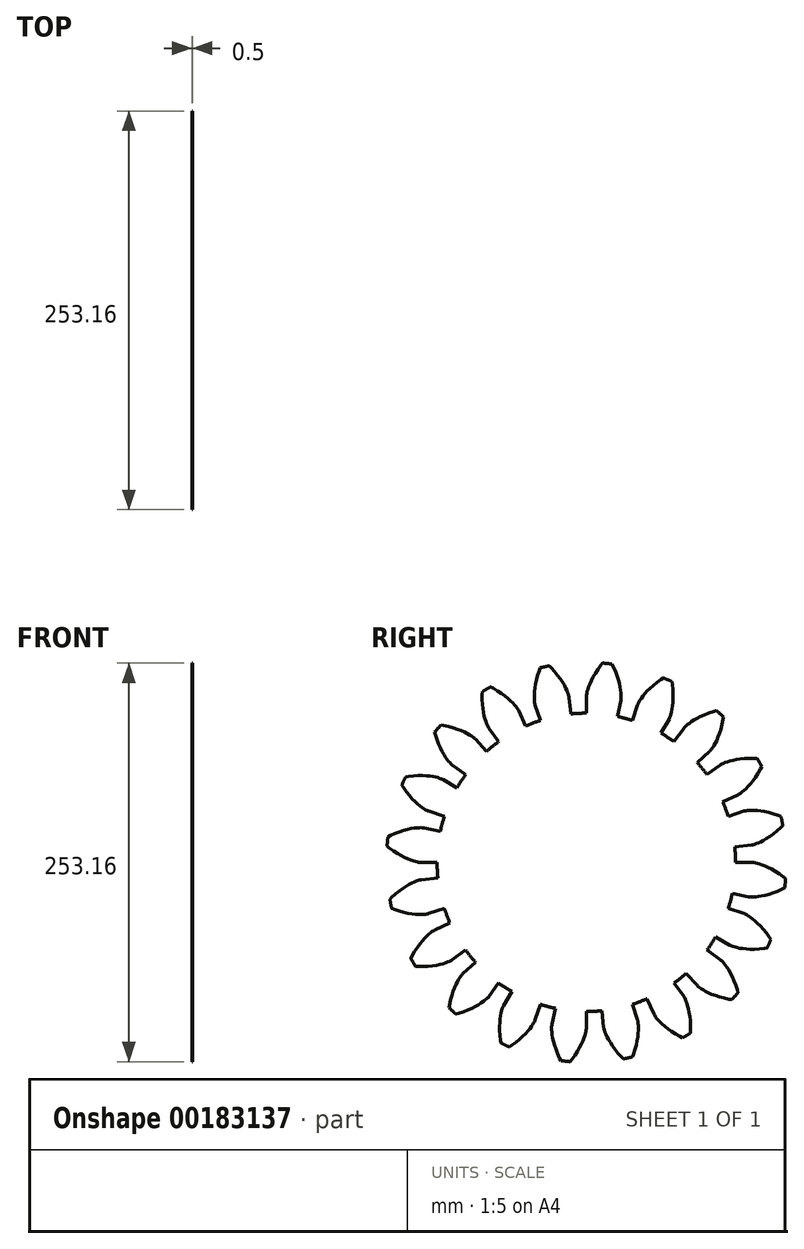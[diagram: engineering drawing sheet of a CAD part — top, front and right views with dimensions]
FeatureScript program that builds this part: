
annotation { "Feature Type Name" : "Feature", "Feature Type Description" : "" }
export const myFeature = defineFeature(function(context is Context, id is Id, definition is map)
    precondition{}
    {
        {
            assignVariable(context, id + "F0", {"name" : "GearThickness", "anyValue" : .5});
        }
        {
            var Q0;
            Q0=qCreatedBy(makeId("Right.planeOp"),FACE);
            var sketch = newSketch(context, id + "F1", { "sketchPlane" : qUnion([Q0])});
            skCircle(sketch, "E0", {"center": v(0, 0) * mm, "radius": 94.77 * mm});
            skCircle(sketch, "E1", {"center": v(0, 0) * mm, "radius": 105.3 * mm, "construction": true});
            skCircle(sketch, "E2", {"center": v(0, 0) * mm, "radius": 112.06 * mm, "construction": true});
            skCircle(sketch, "E3", {"center": v(0, 0) * mm, "radius": 127 * mm});
            skLineSegment(sketch, "E4", {"start": v(0, 0) * mm, "end": v(-105.3, 0) * mm, "construction": true});
            skLineSegment(sketch, "E5.1.0", {"start": v(0, 0) * mm, "end": v(-105.17, 5.26) * mm, "construction": true});
            skLineSegment(sketch, "E5.2.0", {"start": v(0, 0) * mm, "end": v(-104.77, 10.51) * mm, "construction": true});
            skLineSegment(sketch, "E5.3.0", {"start": v(0, 0) * mm, "end": v(-104.12, 15.74) * mm, "construction": true});
            skLineSegment(sketch, "E5.4.0", {"start": v(0, 0) * mm, "end": v(-103.2, 20.92) * mm, "construction": true});
            skLineSegment(sketch, "E5.5.0", {"start": v(0, 0) * mm, "end": v(-102.03, 26.05) * mm, "construction": true});
            skLineSegment(sketch, "E5.6.0", {"start": v(0, 0) * mm, "end": v(-100.6, 31.12) * mm, "construction": true});
            skLineSegment(sketch, "E5.7.0", {"start": v(0, 0) * mm, "end": v(-98.92, 36.1) * mm, "construction": true});
            skLineSegment(sketch, "E5.8.0", {"start": v(0, 0) * mm, "end": v(-96.99, 41) * mm, "construction": true});
            skLineSegment(sketch, "E5.9.0", {"start": v(0, 0) * mm, "end": v(-94.82, 45.8) * mm, "construction": true});
            skLineSegment(sketch, "E5.10.0", {"start": v(0, 0) * mm, "end": v(-92.41, 50.48) * mm, "construction": true});
            skLineSegment(sketch, "E5.11.0", {"start": v(0, 0) * mm, "end": v(-89.77, 55.04) * mm, "construction": true});
            skLineSegment(sketch, "E5.12.0", {"start": v(0, 0) * mm, "end": v(-86.9, 59.46) * mm, "construction": true});
            skLineSegment(sketch, "E5.13.0", {"start": v(0, 0) * mm, "end": v(-83.83, 63.73) * mm, "construction": true});
            skLineSegment(sketch, "E5.14.0", {"start": v(0, 0) * mm, "end": v(-80.54, 67.84) * mm, "construction": true});
            skLineSegment(sketch, "E5.anchor2", {"start": v(0, 0) * mm, "end": v(-80.54, 67.84) * mm, "construction": true});
            skLineSegment(sketch, "E6", {"start": v(-105.17, 5.26) * mm, "end": v(-105.43, 0) * mm, "construction": true});
            skLineSegment(sketch, "E7", {"start": v(-104.77, 10.51) * mm, "end": v(-105.83, 0.04) * mm, "construction": true});
            skLineSegment(sketch, "E8", {"start": v(-104.12, 15.74) * mm, "end": v(-106.48, 0.12) * mm, "construction": true});
            skLineSegment(sketch, "E9", {"start": v(-102.03, 26.05) * mm, "end": v(-108.54, 0.55) * mm, "construction": true});
            skLineSegment(sketch, "E10", {"start": v(-100.6, 31.12) * mm, "end": v(-109.93, 0.94) * mm, "construction": true});
            skLineSegment(sketch, "E11", {"start": v(-98.92, 36.1) * mm, "end": v(-111.55, 1.49) * mm, "construction": true});
            skLineSegment(sketch, "E12", {"start": v(-96.99, 41) * mm, "end": v(-113.4, 2.21) * mm, "construction": true});
            skLineSegment(sketch, "E13", {"start": v(-94.82, 45.8) * mm, "end": v(-115.43, 3.13) * mm, "construction": true});
            skLineSegment(sketch, "E14", {"start": v(-92.41, 50.48) * mm, "end": v(-117.65, 4.28) * mm, "construction": true});
            skLineSegment(sketch, "E15", {"start": v(-89.77, 55.04) * mm, "end": v(-120.04, 5.67) * mm, "construction": true});
            skLineSegment(sketch, "E16", {"start": v(-103.2, 20.92) * mm, "end": v(-107.39, 0.28) * mm, "construction": true});
            skLineSegment(sketch, "E17", {"start": v(-86.9, 59.46) * mm, "end": v(-122.58, 7.31) * mm, "construction": true});
            skLineSegment(sketch, "E18", {"start": v(-83.83, 63.73) * mm, "end": v(-125.25, 9.24) * mm, "construction": true});
            skLineSegment(sketch, "E19", {"start": v(-80.54, 67.84) * mm, "end": v(-128.02, 11.46) * mm, "construction": true});
            skLineSegment(sketch, "E20", {"start": v(0, 0) * mm, "end": v(-104.72, 11) * mm, "construction": true});
            skLineSegment(sketch, "E21", {"start": v(-94.77, 0) * mm, "end": v(-105.3, 0) * mm});
            skLineSegment(sketch, "E22.MirrorCS", {"start": v(-92.7, 19.7) * mm, "end": v(-103, 21.9) * mm});
            skLineSegment(sketch, "E23", {"start": v(-105.3, 0) * mm, "end": v(-105.43, 0) * mm});
            skLineSegment(sketch, "E24", {"start": v(-105.43, 0) * mm, "end": v(-105.83, 0.04) * mm});
            skLineSegment(sketch, "E25", {"start": v(-105.83, 0.04) * mm, "end": v(-106.48, 0.12) * mm});
            skLineSegment(sketch, "E26", {"start": v(-106.48, 0.12) * mm, "end": v(-107.39, 0.28) * mm});
            skLineSegment(sketch, "E27", {"start": v(-107.39, 0.28) * mm, "end": v(-108.54, 0.55) * mm});
            skLineSegment(sketch, "E28", {"start": v(-108.54, 0.55) * mm, "end": v(-109.93, 0.94) * mm});
            skLineSegment(sketch, "E29", {"start": v(-109.93, 0.94) * mm, "end": v(-111.55, 1.49) * mm});
            skLineSegment(sketch, "E30", {"start": v(-111.55, 1.49) * mm, "end": v(-113.4, 2.21) * mm});
            skLineSegment(sketch, "E31", {"start": v(-113.4, 2.21) * mm, "end": v(-115.43, 3.13) * mm});
            skLineSegment(sketch, "E32", {"start": v(-115.43, 3.13) * mm, "end": v(-117.65, 4.28) * mm});
            skLineSegment(sketch, "E33", {"start": v(-117.65, 4.28) * mm, "end": v(-120.04, 5.67) * mm});
            skLineSegment(sketch, "E34", {"start": v(-120.04, 5.67) * mm, "end": v(-122.58, 7.31) * mm});
            skLineSegment(sketch, "E35", {"start": v(-122.58, 7.31) * mm, "end": v(-125.25, 9.24) * mm});
            skLineSegment(sketch, "E36", {"start": v(-125.25, 9.24) * mm, "end": v(-128.02, 11.46) * mm});
            skLineSegment(sketch, "E37.MirrorCS", {"start": v(-103, 21.9) * mm, "end": v(-103.13, 21.92) * mm});
            skLineSegment(sketch, "E38.MirrorCS", {"start": v(-103.13, 21.92) * mm, "end": v(-103.52, 21.97) * mm});
            skLineSegment(sketch, "E39.MirrorCS", {"start": v(-103.52, 21.97) * mm, "end": v(-104.18, 22.02) * mm});
            skLineSegment(sketch, "E40.MirrorCS", {"start": v(-104.18, 22.02) * mm, "end": v(-105.1, 22.05) * mm});
            skLineSegment(sketch, "E41.MirrorCS", {"start": v(-106.28, 22.03) * mm, "end": v(-107.73, 21.94) * mm});
            skLineSegment(sketch, "E42.MirrorCS", {"start": v(-107.73, 21.94) * mm, "end": v(-109.43, 21.74) * mm});
            skLineSegment(sketch, "E43.MirrorCS", {"start": v(-109.43, 21.74) * mm, "end": v(-111.37, 21.41) * mm});
            skLineSegment(sketch, "E44.MirrorCS", {"start": v(-111.37, 21.41) * mm, "end": v(-113.56, 20.93) * mm});
            skLineSegment(sketch, "E45.MirrorCS", {"start": v(-115.97, 20.28) * mm, "end": v(-118.6, 19.42) * mm});
            skLineSegment(sketch, "E46.MirrorCS", {"start": v(-113.56, 20.93) * mm, "end": v(-115.97, 20.28) * mm});
            skLineSegment(sketch, "E47.MirrorCS", {"start": v(-118.6, 19.42) * mm, "end": v(-121.42, 18.33) * mm});
            skLineSegment(sketch, "E48.MirrorCS", {"start": v(-121.42, 18.33) * mm, "end": v(-124.43, 17) * mm});
            skLineSegment(sketch, "E49.MirrorCS", {"start": v(-124.43, 17) * mm, "end": v(-127.6, 15.4) * mm});
            skLineSegment(sketch, "E50.MirrorCS", {"start": v(-105.1, 22.05) * mm, "end": v(-106.28, 22.03) * mm});
            skLineSegment(sketch, "E51.1.0", {"start": v(-90.13, -29.29) * mm, "end": v(-100.15, -32.54) * mm});
            skLineSegment(sketch, "E51.1.1", {"start": v(-118.8, -18.18) * mm, "end": v(-121.15, -20.09) * mm});
            skLineSegment(sketch, "E51.1.2", {"start": v(-94.25, -9.9) * mm, "end": v(-104.72, -11) * mm});
            skLineSegment(sketch, "E51.1.3", {"start": v(-116.56, -16.55) * mm, "end": v(-118.8, -18.18) * mm});
            skLineSegment(sketch, "E51.1.4", {"start": v(-113.22, -32.29) * mm, "end": v(-115.92, -31.7) * mm});
            skLineSegment(sketch, "E51.1.5", {"start": v(-115.92, -31.7) * mm, "end": v(-118.84, -30.93) * mm});
            skLineSegment(sketch, "E51.1.6", {"start": v(-114.47, -15.18) * mm, "end": v(-116.56, -16.55) * mm});
            skLineSegment(sketch, "E51.1.7", {"start": v(-123.6, -22.28) * mm, "end": v(-126.13, -24.78) * mm});
            skLineSegment(sketch, "E51.1.8", {"start": v(-112.54, -14.05) * mm, "end": v(-114.47, -15.18) * mm});
            skLineSegment(sketch, "E51.1.9", {"start": v(-121.98, -29.92) * mm, "end": v(-125.3, -28.66) * mm});
            skLineSegment(sketch, "E51.1.10", {"start": v(-121.15, -20.09) * mm, "end": v(-123.6, -22.28) * mm});
            skLineSegment(sketch, "E51.1.11", {"start": v(-110.75, -32.69) * mm, "end": v(-113.22, -32.29) * mm});
            skLineSegment(sketch, "E51.1.12", {"start": v(-118.84, -30.93) * mm, "end": v(-121.98, -29.92) * mm});
            skLineSegment(sketch, "E51.1.13", {"start": v(-107.89, -11.89) * mm, "end": v(-109.23, -12.43) * mm});
            skLineSegment(sketch, "E51.1.14", {"start": v(-109.23, -12.43) * mm, "end": v(-110.79, -13.14) * mm});
            skLineSegment(sketch, "E51.1.15", {"start": v(-110.79, -13.14) * mm, "end": v(-112.54, -14.05) * mm});
            skLineSegment(sketch, "E51.1.16", {"start": v(-106.55, -33.06) * mm, "end": v(-108.52, -32.94) * mm});
            skLineSegment(sketch, "E51.1.17", {"start": v(-104.84, -33.08) * mm, "end": v(-106.55, -33.06) * mm});
            skLineSegment(sketch, "E51.1.18", {"start": v(-108.52, -32.94) * mm, "end": v(-110.75, -32.69) * mm});
            skLineSegment(sketch, "E51.1.19", {"start": v(-106.77, -11.5) * mm, "end": v(-107.89, -11.89) * mm});
            skLineSegment(sketch, "E51.1.20", {"start": v(-105.88, -11.25) * mm, "end": v(-106.77, -11.5) * mm});
            skLineSegment(sketch, "E51.1.21", {"start": v(-103.4, -33.02) * mm, "end": v(-104.84, -33.08) * mm});
            skLineSegment(sketch, "E51.1.22", {"start": v(-102.22, -32.92) * mm, "end": v(-103.4, -33.02) * mm});
            skLineSegment(sketch, "E51.1.23", {"start": v(-100.66, -32.67) * mm, "end": v(-101.3, -32.8) * mm});
            skLineSegment(sketch, "E51.1.24", {"start": v(-104.72, -11) * mm, "end": v(-104.85, -11.03) * mm});
            skLineSegment(sketch, "E51.1.25", {"start": v(-104.85, -11.03) * mm, "end": v(-105.24, -11.1) * mm});
            skLineSegment(sketch, "E51.1.26", {"start": v(-101.3, -32.8) * mm, "end": v(-102.22, -32.92) * mm});
            skLineSegment(sketch, "E51.1.27", {"start": v(-105.24, -11.1) * mm, "end": v(-105.88, -11.25) * mm});
            skLineSegment(sketch, "E51.1.28", {"start": v(-100.27, -32.58) * mm, "end": v(-100.66, -32.67) * mm});
            skLineSegment(sketch, "E51.1.29", {"start": v(-100.15, -32.54) * mm, "end": v(-100.27, -32.58) * mm});
            skLineSegment(sketch, "E51.2.0", {"start": v(-76.67, -55.7) * mm, "end": v(-85.2, -61.9) * mm});
            skLineSegment(sketch, "E51.2.1", {"start": v(-107.36, -54) * mm, "end": v(-109.01, -56.54) * mm});
            skLineSegment(sketch, "E51.2.2", {"start": v(-86.58, -38.55) * mm, "end": v(-96.2, -42.83) * mm});
            skLineSegment(sketch, "E51.2.3", {"start": v(-105.74, -51.76) * mm, "end": v(-107.36, -54) * mm});
            skLineSegment(sketch, "E51.2.4", {"start": v(-97.7, -65.7) * mm, "end": v(-100.45, -65.98) * mm});
            skLineSegment(sketch, "E51.2.5", {"start": v(-100.45, -65.98) * mm, "end": v(-103.47, -66.14) * mm});
            skLineSegment(sketch, "E51.2.6", {"start": v(-104.17, -49.81) * mm, "end": v(-105.74, -51.76) * mm});
            skLineSegment(sketch, "E51.2.7", {"start": v(-110.66, -59.38) * mm, "end": v(-112.3, -62.54) * mm});
            skLineSegment(sketch, "E51.2.8", {"start": v(-102.69, -48.14) * mm, "end": v(-104.17, -49.81) * mm});
            skLineSegment(sketch, "E51.2.9", {"start": v(-106.76, -66.15) * mm, "end": v(-110.3, -65.98) * mm});
            skLineSegment(sketch, "E51.2.10", {"start": v(-109.01, -56.54) * mm, "end": v(-110.66, -59.38) * mm});
            skLineSegment(sketch, "E51.2.11", {"start": v(-95.23, -65.31) * mm, "end": v(-97.7, -65.7) * mm});
            skLineSegment(sketch, "E51.2.12", {"start": v(-103.47, -66.14) * mm, "end": v(-106.76, -66.15) * mm});
            skLineSegment(sketch, "E51.2.13", {"start": v(-98.93, -44.65) * mm, "end": v(-100.05, -45.57) * mm});
            skLineSegment(sketch, "E51.2.14", {"start": v(-100.05, -45.57) * mm, "end": v(-101.3, -46.73) * mm});
            skLineSegment(sketch, "E51.2.15", {"start": v(-101.3, -46.73) * mm, "end": v(-102.69, -48.14) * mm});
            skLineSegment(sketch, "E51.2.16", {"start": v(-91.12, -64.37) * mm, "end": v(-93.03, -64.86) * mm});
            skLineSegment(sketch, "E51.2.17", {"start": v(-89.49, -63.86) * mm, "end": v(-91.12, -64.37) * mm});
            skLineSegment(sketch, "E51.2.18", {"start": v(-93.03, -64.86) * mm, "end": v(-95.23, -65.31) * mm});
            skLineSegment(sketch, "E51.2.19", {"start": v(-97.99, -43.93) * mm, "end": v(-98.93, -44.65) * mm});
            skLineSegment(sketch, "E51.2.20", {"start": v(-97.23, -43.42) * mm, "end": v(-97.99, -43.93) * mm});
            skLineSegment(sketch, "E51.2.21", {"start": v(-88.13, -63.36) * mm, "end": v(-89.49, -63.86) * mm});
            skLineSegment(sketch, "E51.2.22", {"start": v(-87.04, -62.9) * mm, "end": v(-88.13, -63.36) * mm});
            skLineSegment(sketch, "E51.2.23", {"start": v(-85.64, -62.17) * mm, "end": v(-86.21, -62.5) * mm});
            skLineSegment(sketch, "E51.2.24", {"start": v(-96.2, -42.83) * mm, "end": v(-96.32, -42.89) * mm});
            skLineSegment(sketch, "E51.2.25", {"start": v(-96.32, -42.89) * mm, "end": v(-96.66, -43.08) * mm});
            skLineSegment(sketch, "E51.2.26", {"start": v(-86.21, -62.5) * mm, "end": v(-87.04, -62.9) * mm});
            skLineSegment(sketch, "E51.2.27", {"start": v(-96.66, -43.08) * mm, "end": v(-97.23, -43.42) * mm});
            skLineSegment(sketch, "E51.2.28", {"start": v(-85.3, -61.97) * mm, "end": v(-85.64, -62.17) * mm});
            skLineSegment(sketch, "E51.2.29", {"start": v(-85.2, -61.9) * mm, "end": v(-85.3, -61.97) * mm});
            skLineSegment(sketch, "E51.3.0", {"start": v(-55.7, -76.67) * mm, "end": v(-61.9, -85.2) * mm});
            skLineSegment(sketch, "E51.3.1", {"start": v(-85.42, -84.53) * mm, "end": v(-86.2, -87.46) * mm});
            skLineSegment(sketch, "E51.3.2", {"start": v(-70.43, -63.41) * mm, "end": v(-78.25, -70.46) * mm});
            skLineSegment(sketch, "E51.3.3", {"start": v(-84.57, -81.9) * mm, "end": v(-85.42, -84.53) * mm});
            skLineSegment(sketch, "E51.3.4", {"start": v(-72.62, -92.67) * mm, "end": v(-75.14, -93.79) * mm});
            skLineSegment(sketch, "E51.3.5", {"start": v(-75.14, -93.79) * mm, "end": v(-77.97, -94.87) * mm});
            skLineSegment(sketch, "E51.3.6", {"start": v(-83.68, -79.57) * mm, "end": v(-84.57, -81.9) * mm});
            skLineSegment(sketch, "E51.3.7", {"start": v(-86.9, -90.67) * mm, "end": v(-87.47, -94.18) * mm});
            skLineSegment(sketch, "E51.3.8", {"start": v(-82.79, -77.52) * mm, "end": v(-83.68, -79.57) * mm});
            skLineSegment(sketch, "E51.3.9", {"start": v(-81.1, -95.9) * mm, "end": v(-84.52, -96.84) * mm});
            skLineSegment(sketch, "E51.3.10", {"start": v(-86.2, -87.46) * mm, "end": v(-86.9, -90.67) * mm});
            skLineSegment(sketch, "E51.3.11", {"start": v(-70.38, -91.54) * mm, "end": v(-72.62, -92.67) * mm});
            skLineSegment(sketch, "E51.3.12", {"start": v(-77.97, -94.87) * mm, "end": v(-81.1, -95.9) * mm});
            skLineSegment(sketch, "E51.3.13", {"start": v(-80.3, -73.03) * mm, "end": v(-81.07, -74.26) * mm});
            skLineSegment(sketch, "E51.3.14", {"start": v(-81.07, -74.26) * mm, "end": v(-81.9, -75.75) * mm});
            skLineSegment(sketch, "E51.3.15", {"start": v(-81.9, -75.75) * mm, "end": v(-82.79, -77.52) * mm});
            skLineSegment(sketch, "E51.3.16", {"start": v(-66.77, -89.38) * mm, "end": v(-68.44, -90.44) * mm});
            skLineSegment(sketch, "E51.3.17", {"start": v(-65.38, -88.39) * mm, "end": v(-66.77, -89.38) * mm});
            skLineSegment(sketch, "E51.3.18", {"start": v(-68.44, -90.44) * mm, "end": v(-70.38, -91.54) * mm});
            skLineSegment(sketch, "E51.3.19", {"start": v(-79.62, -72.06) * mm, "end": v(-80.3, -73.03) * mm});
            skLineSegment(sketch, "E51.3.20", {"start": v(-79.05, -71.34) * mm, "end": v(-79.62, -72.06) * mm});
            skLineSegment(sketch, "E51.3.21", {"start": v(-64.24, -87.5) * mm, "end": v(-65.38, -88.39) * mm});
            skLineSegment(sketch, "E51.3.22", {"start": v(-63.35, -86.71) * mm, "end": v(-64.24, -87.5) * mm});
            skLineSegment(sketch, "E51.3.23", {"start": v(-62.23, -85.6) * mm, "end": v(-62.68, -86.07) * mm});
            skLineSegment(sketch, "E51.3.24", {"start": v(-78.25, -70.46) * mm, "end": v(-78.35, -70.55) * mm});
            skLineSegment(sketch, "E51.3.25", {"start": v(-78.35, -70.55) * mm, "end": v(-78.62, -70.84) * mm});
            skLineSegment(sketch, "E51.3.26", {"start": v(-62.68, -86.07) * mm, "end": v(-63.35, -86.71) * mm});
            skLineSegment(sketch, "E51.3.27", {"start": v(-78.62, -70.84) * mm, "end": v(-79.05, -71.34) * mm});
            skLineSegment(sketch, "E51.3.28", {"start": v(-61.98, -85.3) * mm, "end": v(-62.23, -85.6) * mm});
            skLineSegment(sketch, "E51.3.29", {"start": v(-61.9, -85.2) * mm, "end": v(-61.98, -85.3) * mm});
            skLineSegment(sketch, "E51.4.0", {"start": v(-29.29, -90.13) * mm, "end": v(-32.54, -100.15) * mm});
            skLineSegment(sketch, "E51.4.1", {"start": v(-55.12, -106.8) * mm, "end": v(-54.96, -109.82) * mm});
            skLineSegment(sketch, "E51.4.2", {"start": v(-47.39, -82.07) * mm, "end": v(-52.65, -91.2) * mm});
            skLineSegment(sketch, "E51.4.3", {"start": v(-55.12, -104.03) * mm, "end": v(-55.12, -106.8) * mm});
            skLineSegment(sketch, "E51.4.4", {"start": v(-40.43, -110.57) * mm, "end": v(-42.48, -112.42) * mm});
            skLineSegment(sketch, "E51.4.5", {"start": v(-42.48, -112.42) * mm, "end": v(-44.83, -114.32) * mm});
            skLineSegment(sketch, "E51.4.6", {"start": v(-55, -101.53) * mm, "end": v(-55.12, -104.03) * mm});
            skLineSegment(sketch, "E51.4.7", {"start": v(-54.62, -113.09) * mm, "end": v(-54.09, -116.6) * mm});
            skLineSegment(sketch, "E51.4.8", {"start": v(-54.78, -99.3) * mm, "end": v(-55, -101.53) * mm});
            skLineSegment(sketch, "E51.4.9", {"start": v(-47.5, -116.27) * mm, "end": v(-50.46, -118.22) * mm});
            skLineSegment(sketch, "E51.4.10", {"start": v(-54.96, -109.82) * mm, "end": v(-54.62, -113.09) * mm});
            skLineSegment(sketch, "E51.4.11", {"start": v(-38.65, -108.81) * mm, "end": v(-40.43, -110.57) * mm});
            skLineSegment(sketch, "E51.4.12", {"start": v(-44.83, -114.32) * mm, "end": v(-47.5, -116.27) * mm});
            skLineSegment(sketch, "E51.4.13", {"start": v(-53.8, -94.27) * mm, "end": v(-54.15, -95.67) * mm});
            skLineSegment(sketch, "E51.4.14", {"start": v(-54.15, -95.67) * mm, "end": v(-54.49, -97.35) * mm});
            skLineSegment(sketch, "E51.4.15", {"start": v(-54.49, -97.35) * mm, "end": v(-54.78, -99.3) * mm});
            skLineSegment(sketch, "E51.4.16", {"start": v(-35.89, -105.64) * mm, "end": v(-37.14, -107.16) * mm});
            skLineSegment(sketch, "E51.4.17", {"start": v(-34.86, -104.26) * mm, "end": v(-35.89, -105.64) * mm});
            skLineSegment(sketch, "E51.4.18", {"start": v(-37.14, -107.16) * mm, "end": v(-38.65, -108.81) * mm});
            skLineSegment(sketch, "E51.4.19", {"start": v(-53.45, -93.14) * mm, "end": v(-53.8, -94.27) * mm});
            skLineSegment(sketch, "E51.4.20", {"start": v(-53.14, -92.27) * mm, "end": v(-53.45, -93.14) * mm});
            skLineSegment(sketch, "E51.4.21", {"start": v(-34.06, -103.06) * mm, "end": v(-34.86, -104.26) * mm});
            skLineSegment(sketch, "E51.4.22", {"start": v(-33.45, -102.04) * mm, "end": v(-34.06, -103.06) * mm});
            skLineSegment(sketch, "E51.4.23", {"start": v(-32.74, -100.64) * mm, "end": v(-33.02, -101.23) * mm});
            skLineSegment(sketch, "E51.4.24", {"start": v(-52.65, -91.2) * mm, "end": v(-52.71, -91.3) * mm});
            skLineSegment(sketch, "E51.4.25", {"start": v(-52.71, -91.3) * mm, "end": v(-52.88, -91.67) * mm});
            skLineSegment(sketch, "E51.4.26", {"start": v(-33.02, -101.23) * mm, "end": v(-33.45, -102.04) * mm});
            skLineSegment(sketch, "E51.4.27", {"start": v(-52.88, -91.67) * mm, "end": v(-53.14, -92.27) * mm});
            skLineSegment(sketch, "E51.4.28", {"start": v(-32.58, -100.27) * mm, "end": v(-32.74, -100.64) * mm});
            skLineSegment(sketch, "E51.4.29", {"start": v(-32.54, -100.15) * mm, "end": v(-32.58, -100.27) * mm});
            skLineSegment(sketch, "E51.5.0", {"start": v(0, -94.77) * mm, "end": v(0, -105.3) * mm});
            skLineSegment(sketch, "E51.5.1", {"start": v(-19.42, -118.6) * mm, "end": v(-18.33, -121.42) * mm});
            skLineSegment(sketch, "E51.5.2", {"start": v(-19.7, -92.7) * mm, "end": v(-21.9, -103) * mm});
            skLineSegment(sketch, "E51.5.3", {"start": v(-20.28, -115.97) * mm, "end": v(-19.42, -118.6) * mm});
            skLineSegment(sketch, "E51.5.4", {"start": v(-4.28, -117.65) * mm, "end": v(-5.67, -120.04) * mm});
            skLineSegment(sketch, "E51.5.5", {"start": v(-5.67, -120.04) * mm, "end": v(-7.31, -122.58) * mm});
            skLineSegment(sketch, "E51.5.6", {"start": v(-20.93, -113.56) * mm, "end": v(-20.28, -115.97) * mm});
            skLineSegment(sketch, "E51.5.7", {"start": v(-17, -124.43) * mm, "end": v(-15.4, -127.6) * mm});
            skLineSegment(sketch, "E51.5.8", {"start": v(-21.41, -111.37) * mm, "end": v(-20.93, -113.56) * mm});
            skLineSegment(sketch, "E51.5.9", {"start": v(-9.24, -125.25) * mm, "end": v(-11.46, -128.02) * mm});
            skLineSegment(sketch, "E51.5.10", {"start": v(-18.33, -121.42) * mm, "end": v(-17, -124.43) * mm});
            skLineSegment(sketch, "E51.5.11", {"start": v(-3.13, -115.43) * mm, "end": v(-4.28, -117.65) * mm});
            skLineSegment(sketch, "E51.5.12", {"start": v(-7.31, -122.58) * mm, "end": v(-9.24, -125.25) * mm});
            skLineSegment(sketch, "E51.5.13", {"start": v(-22.03, -106.28) * mm, "end": v(-21.94, -107.73) * mm});
            skLineSegment(sketch, "E51.5.14", {"start": v(-21.94, -107.73) * mm, "end": v(-21.74, -109.43) * mm});
            skLineSegment(sketch, "E51.5.15", {"start": v(-21.74, -109.43) * mm, "end": v(-21.41, -111.37) * mm});
            skLineSegment(sketch, "E51.5.16", {"start": v(-1.49, -111.55) * mm, "end": v(-2.21, -113.4) * mm});
            skLineSegment(sketch, "E51.5.17", {"start": v(-0.94, -109.93) * mm, "end": v(-1.49, -111.55) * mm});
            skLineSegment(sketch, "E51.5.18", {"start": v(-2.21, -113.4) * mm, "end": v(-3.13, -115.43) * mm});
            skLineSegment(sketch, "E51.5.19", {"start": v(-22.05, -105.1) * mm, "end": v(-22.03, -106.28) * mm});
            skLineSegment(sketch, "E51.5.20", {"start": v(-22.02, -104.18) * mm, "end": v(-22.05, -105.1) * mm});
            skLineSegment(sketch, "E51.5.21", {"start": v(-0.55, -108.54) * mm, "end": v(-0.94, -109.93) * mm});
            skLineSegment(sketch, "E51.5.22", {"start": v(-0.28, -107.39) * mm, "end": v(-0.55, -108.54) * mm});
            skLineSegment(sketch, "E51.5.23", {"start": v(-0.04, -105.83) * mm, "end": v(-0.12, -106.48) * mm});
            skLineSegment(sketch, "E51.5.24", {"start": v(-21.9, -103) * mm, "end": v(-21.92, -103.13) * mm});
            skLineSegment(sketch, "E51.5.25", {"start": v(-21.92, -103.13) * mm, "end": v(-21.97, -103.52) * mm});
            skLineSegment(sketch, "E51.5.26", {"start": v(-0.12, -106.48) * mm, "end": v(-0.28, -107.39) * mm});
            skLineSegment(sketch, "E51.5.27", {"start": v(-21.97, -103.52) * mm, "end": v(-22.02, -104.18) * mm});
            skLineSegment(sketch, "E51.5.28", {"start": v(0, -105.43) * mm, "end": v(-0.04, -105.83) * mm});
            skLineSegment(sketch, "E51.5.29", {"start": v(0, -105.3) * mm, "end": v(0, -105.43) * mm});
            skLineSegment(sketch, "E51.6.0", {"start": v(29.29, -90.13) * mm, "end": v(32.54, -100.15) * mm});
            skLineSegment(sketch, "E51.6.1", {"start": v(18.18, -118.8) * mm, "end": v(20.09, -121.15) * mm});
            skLineSegment(sketch, "E51.6.2", {"start": v(9.9, -94.25) * mm, "end": v(11, -104.72) * mm});
            skLineSegment(sketch, "E51.6.3", {"start": v(16.55, -116.56) * mm, "end": v(18.18, -118.8) * mm});
            skLineSegment(sketch, "E51.6.4", {"start": v(32.29, -113.22) * mm, "end": v(31.7, -115.92) * mm});
            skLineSegment(sketch, "E51.6.5", {"start": v(31.7, -115.92) * mm, "end": v(30.93, -118.84) * mm});
            skLineSegment(sketch, "E51.6.6", {"start": v(15.18, -114.47) * mm, "end": v(16.55, -116.56) * mm});
            skLineSegment(sketch, "E51.6.7", {"start": v(22.28, -123.6) * mm, "end": v(24.78, -126.13) * mm});
            skLineSegment(sketch, "E51.6.8", {"start": v(14.05, -112.54) * mm, "end": v(15.18, -114.47) * mm});
            skLineSegment(sketch, "E51.6.9", {"start": v(29.92, -121.98) * mm, "end": v(28.66, -125.3) * mm});
            skLineSegment(sketch, "E51.6.10", {"start": v(20.09, -121.15) * mm, "end": v(22.28, -123.6) * mm});
            skLineSegment(sketch, "E51.6.11", {"start": v(32.69, -110.75) * mm, "end": v(32.29, -113.22) * mm});
            skLineSegment(sketch, "E51.6.12", {"start": v(30.93, -118.84) * mm, "end": v(29.92, -121.98) * mm});
            skLineSegment(sketch, "E51.6.13", {"start": v(11.89, -107.89) * mm, "end": v(12.43, -109.23) * mm});
            skLineSegment(sketch, "E51.6.14", {"start": v(12.43, -109.23) * mm, "end": v(13.14, -110.79) * mm});
            skLineSegment(sketch, "E51.6.15", {"start": v(13.14, -110.79) * mm, "end": v(14.05, -112.54) * mm});
            skLineSegment(sketch, "E51.6.16", {"start": v(33.06, -106.55) * mm, "end": v(32.94, -108.52) * mm});
            skLineSegment(sketch, "E51.6.17", {"start": v(33.08, -104.84) * mm, "end": v(33.06, -106.55) * mm});
            skLineSegment(sketch, "E51.6.18", {"start": v(32.94, -108.52) * mm, "end": v(32.69, -110.75) * mm});
            skLineSegment(sketch, "E51.6.19", {"start": v(11.5, -106.77) * mm, "end": v(11.89, -107.89) * mm});
            skLineSegment(sketch, "E51.6.20", {"start": v(11.25, -105.88) * mm, "end": v(11.5, -106.77) * mm});
            skLineSegment(sketch, "E51.6.21", {"start": v(33.02, -103.4) * mm, "end": v(33.08, -104.84) * mm});
            skLineSegment(sketch, "E51.6.22", {"start": v(32.92, -102.22) * mm, "end": v(33.02, -103.4) * mm});
            skLineSegment(sketch, "E51.6.23", {"start": v(32.67, -100.66) * mm, "end": v(32.8, -101.3) * mm});
            skLineSegment(sketch, "E51.6.24", {"start": v(11, -104.72) * mm, "end": v(11.03, -104.85) * mm});
            skLineSegment(sketch, "E51.6.25", {"start": v(11.03, -104.85) * mm, "end": v(11.1, -105.24) * mm});
            skLineSegment(sketch, "E51.6.26", {"start": v(32.8, -101.3) * mm, "end": v(32.92, -102.22) * mm});
            skLineSegment(sketch, "E51.6.27", {"start": v(11.1, -105.24) * mm, "end": v(11.25, -105.88) * mm});
            skLineSegment(sketch, "E51.6.28", {"start": v(32.58, -100.27) * mm, "end": v(32.67, -100.66) * mm});
            skLineSegment(sketch, "E51.6.29", {"start": v(32.54, -100.15) * mm, "end": v(32.58, -100.27) * mm});
            skLineSegment(sketch, "E51.7.0", {"start": v(55.7, -76.67) * mm, "end": v(61.9, -85.2) * mm});
            skLineSegment(sketch, "E51.7.1", {"start": v(54, -107.36) * mm, "end": v(56.54, -109.01) * mm});
            skLineSegment(sketch, "E51.7.2", {"start": v(38.55, -86.58) * mm, "end": v(42.83, -96.2) * mm});
            skLineSegment(sketch, "E51.7.3", {"start": v(51.76, -105.74) * mm, "end": v(54, -107.36) * mm});
            skLineSegment(sketch, "E51.7.4", {"start": v(65.7, -97.7) * mm, "end": v(65.98, -100.45) * mm});
            skLineSegment(sketch, "E51.7.5", {"start": v(65.98, -100.45) * mm, "end": v(66.14, -103.47) * mm});
            skLineSegment(sketch, "E51.7.6", {"start": v(49.81, -104.17) * mm, "end": v(51.76, -105.74) * mm});
            skLineSegment(sketch, "E51.7.7", {"start": v(59.38, -110.66) * mm, "end": v(62.54, -112.3) * mm});
            skLineSegment(sketch, "E51.7.8", {"start": v(48.14, -102.69) * mm, "end": v(49.81, -104.17) * mm});
            skLineSegment(sketch, "E51.7.9", {"start": v(66.15, -106.76) * mm, "end": v(65.98, -110.3) * mm});
            skLineSegment(sketch, "E51.7.10", {"start": v(56.54, -109.01) * mm, "end": v(59.38, -110.66) * mm});
            skLineSegment(sketch, "E51.7.11", {"start": v(65.31, -95.23) * mm, "end": v(65.7, -97.7) * mm});
            skLineSegment(sketch, "E51.7.12", {"start": v(66.14, -103.47) * mm, "end": v(66.15, -106.76) * mm});
            skLineSegment(sketch, "E51.7.13", {"start": v(44.65, -98.93) * mm, "end": v(45.57, -100.05) * mm});
            skLineSegment(sketch, "E51.7.14", {"start": v(45.57, -100.05) * mm, "end": v(46.73, -101.3) * mm});
            skLineSegment(sketch, "E51.7.15", {"start": v(46.73, -101.3) * mm, "end": v(48.14, -102.69) * mm});
            skLineSegment(sketch, "E51.7.16", {"start": v(64.37, -91.12) * mm, "end": v(64.86, -93.03) * mm});
            skLineSegment(sketch, "E51.7.17", {"start": v(63.86, -89.49) * mm, "end": v(64.37, -91.12) * mm});
            skLineSegment(sketch, "E51.7.18", {"start": v(64.86, -93.03) * mm, "end": v(65.31, -95.23) * mm});
            skLineSegment(sketch, "E51.7.19", {"start": v(43.93, -97.99) * mm, "end": v(44.65, -98.93) * mm});
            skLineSegment(sketch, "E51.7.20", {"start": v(43.42, -97.23) * mm, "end": v(43.93, -97.99) * mm});
            skLineSegment(sketch, "E51.7.21", {"start": v(63.36, -88.13) * mm, "end": v(63.86, -89.49) * mm});
            skLineSegment(sketch, "E51.7.22", {"start": v(62.9, -87.04) * mm, "end": v(63.36, -88.13) * mm});
            skLineSegment(sketch, "E51.7.23", {"start": v(62.17, -85.64) * mm, "end": v(62.5, -86.21) * mm});
            skLineSegment(sketch, "E51.7.24", {"start": v(42.83, -96.2) * mm, "end": v(42.89, -96.32) * mm});
            skLineSegment(sketch, "E51.7.25", {"start": v(42.89, -96.32) * mm, "end": v(43.08, -96.66) * mm});
            skLineSegment(sketch, "E51.7.26", {"start": v(62.5, -86.21) * mm, "end": v(62.9, -87.04) * mm});
            skLineSegment(sketch, "E51.7.27", {"start": v(43.08, -96.66) * mm, "end": v(43.42, -97.23) * mm});
            skLineSegment(sketch, "E51.7.28", {"start": v(61.97, -85.3) * mm, "end": v(62.17, -85.64) * mm});
            skLineSegment(sketch, "E51.7.29", {"start": v(61.9, -85.2) * mm, "end": v(61.97, -85.3) * mm});
            skLineSegment(sketch, "E51.8.0", {"start": v(76.67, -55.7) * mm, "end": v(85.2, -61.9) * mm});
            skLineSegment(sketch, "E51.8.1", {"start": v(84.53, -85.42) * mm, "end": v(87.46, -86.2) * mm});
            skLineSegment(sketch, "E51.8.2", {"start": v(63.41, -70.43) * mm, "end": v(70.46, -78.25) * mm});
            skLineSegment(sketch, "E51.8.3", {"start": v(81.9, -84.57) * mm, "end": v(84.53, -85.42) * mm});
            skLineSegment(sketch, "E51.8.4", {"start": v(92.67, -72.62) * mm, "end": v(93.79, -75.14) * mm});
            skLineSegment(sketch, "E51.8.5", {"start": v(93.79, -75.14) * mm, "end": v(94.87, -77.97) * mm});
            skLineSegment(sketch, "E51.8.6", {"start": v(79.57, -83.68) * mm, "end": v(81.9, -84.57) * mm});
            skLineSegment(sketch, "E51.8.7", {"start": v(90.67, -86.9) * mm, "end": v(94.18, -87.47) * mm});
            skLineSegment(sketch, "E51.8.8", {"start": v(77.52, -82.79) * mm, "end": v(79.57, -83.68) * mm});
            skLineSegment(sketch, "E51.8.9", {"start": v(95.9, -81.1) * mm, "end": v(96.84, -84.52) * mm});
            skLineSegment(sketch, "E51.8.10", {"start": v(87.46, -86.2) * mm, "end": v(90.67, -86.9) * mm});
            skLineSegment(sketch, "E51.8.11", {"start": v(91.54, -70.38) * mm, "end": v(92.67, -72.62) * mm});
            skLineSegment(sketch, "E51.8.12", {"start": v(94.87, -77.97) * mm, "end": v(95.9, -81.1) * mm});
            skLineSegment(sketch, "E51.8.13", {"start": v(73.03, -80.3) * mm, "end": v(74.26, -81.07) * mm});
            skLineSegment(sketch, "E51.8.14", {"start": v(74.26, -81.07) * mm, "end": v(75.75, -81.9) * mm});
            skLineSegment(sketch, "E51.8.15", {"start": v(75.75, -81.9) * mm, "end": v(77.52, -82.79) * mm});
            skLineSegment(sketch, "E51.8.16", {"start": v(89.38, -66.77) * mm, "end": v(90.44, -68.44) * mm});
            skLineSegment(sketch, "E51.8.17", {"start": v(88.39, -65.38) * mm, "end": v(89.38, -66.77) * mm});
            skLineSegment(sketch, "E51.8.18", {"start": v(90.44, -68.44) * mm, "end": v(91.54, -70.38) * mm});
            skLineSegment(sketch, "E51.8.19", {"start": v(72.06, -79.62) * mm, "end": v(73.03, -80.3) * mm});
            skLineSegment(sketch, "E51.8.20", {"start": v(71.34, -79.05) * mm, "end": v(72.06, -79.62) * mm});
            skLineSegment(sketch, "E51.8.21", {"start": v(87.5, -64.24) * mm, "end": v(88.39, -65.38) * mm});
            skLineSegment(sketch, "E51.8.22", {"start": v(86.71, -63.35) * mm, "end": v(87.5, -64.24) * mm});
            skLineSegment(sketch, "E51.8.23", {"start": v(85.6, -62.23) * mm, "end": v(86.07, -62.68) * mm});
            skLineSegment(sketch, "E51.8.24", {"start": v(70.46, -78.25) * mm, "end": v(70.55, -78.35) * mm});
            skLineSegment(sketch, "E51.8.25", {"start": v(70.55, -78.35) * mm, "end": v(70.84, -78.62) * mm});
            skLineSegment(sketch, "E51.8.26", {"start": v(86.07, -62.68) * mm, "end": v(86.71, -63.35) * mm});
            skLineSegment(sketch, "E51.8.27", {"start": v(70.84, -78.62) * mm, "end": v(71.34, -79.05) * mm});
            skLineSegment(sketch, "E51.8.28", {"start": v(85.3, -61.98) * mm, "end": v(85.6, -62.23) * mm});
            skLineSegment(sketch, "E51.8.29", {"start": v(85.2, -61.9) * mm, "end": v(85.3, -61.98) * mm});
            skLineSegment(sketch, "E51.9.0", {"start": v(90.13, -29.29) * mm, "end": v(100.15, -32.54) * mm});
            skLineSegment(sketch, "E51.9.1", {"start": v(106.8, -55.12) * mm, "end": v(109.82, -54.96) * mm});
            skLineSegment(sketch, "E51.9.2", {"start": v(82.07, -47.39) * mm, "end": v(91.2, -52.65) * mm});
            skLineSegment(sketch, "E51.9.3", {"start": v(104.03, -55.12) * mm, "end": v(106.8, -55.12) * mm});
            skLineSegment(sketch, "E51.9.4", {"start": v(110.57, -40.43) * mm, "end": v(112.42, -42.48) * mm});
            skLineSegment(sketch, "E51.9.5", {"start": v(112.42, -42.48) * mm, "end": v(114.32, -44.83) * mm});
            skLineSegment(sketch, "E51.9.6", {"start": v(101.53, -55) * mm, "end": v(104.03, -55.12) * mm});
            skLineSegment(sketch, "E51.9.7", {"start": v(113.09, -54.62) * mm, "end": v(116.6, -54.09) * mm});
            skLineSegment(sketch, "E51.9.8", {"start": v(99.3, -54.78) * mm, "end": v(101.53, -55) * mm});
            skLineSegment(sketch, "E51.9.9", {"start": v(116.27, -47.5) * mm, "end": v(118.22, -50.46) * mm});
            skLineSegment(sketch, "E51.9.10", {"start": v(109.82, -54.96) * mm, "end": v(113.09, -54.62) * mm});
            skLineSegment(sketch, "E51.9.11", {"start": v(108.81, -38.65) * mm, "end": v(110.57, -40.43) * mm});
            skLineSegment(sketch, "E51.9.12", {"start": v(114.32, -44.83) * mm, "end": v(116.27, -47.5) * mm});
            skLineSegment(sketch, "E51.9.13", {"start": v(94.27, -53.8) * mm, "end": v(95.67, -54.15) * mm});
            skLineSegment(sketch, "E51.9.14", {"start": v(95.67, -54.15) * mm, "end": v(97.35, -54.49) * mm});
            skLineSegment(sketch, "E51.9.15", {"start": v(97.35, -54.49) * mm, "end": v(99.3, -54.78) * mm});
            skLineSegment(sketch, "E51.9.16", {"start": v(105.64, -35.89) * mm, "end": v(107.16, -37.14) * mm});
            skLineSegment(sketch, "E51.9.17", {"start": v(104.26, -34.86) * mm, "end": v(105.64, -35.89) * mm});
            skLineSegment(sketch, "E51.9.18", {"start": v(107.16, -37.14) * mm, "end": v(108.81, -38.65) * mm});
            skLineSegment(sketch, "E51.9.19", {"start": v(93.14, -53.45) * mm, "end": v(94.27, -53.8) * mm});
            skLineSegment(sketch, "E51.9.20", {"start": v(92.27, -53.14) * mm, "end": v(93.14, -53.45) * mm});
            skLineSegment(sketch, "E51.9.21", {"start": v(103.06, -34.06) * mm, "end": v(104.26, -34.86) * mm});
            skLineSegment(sketch, "E51.9.22", {"start": v(102.04, -33.45) * mm, "end": v(103.06, -34.06) * mm});
            skLineSegment(sketch, "E51.9.23", {"start": v(100.64, -32.74) * mm, "end": v(101.23, -33.02) * mm});
            skLineSegment(sketch, "E51.9.24", {"start": v(91.2, -52.65) * mm, "end": v(91.3, -52.71) * mm});
            skLineSegment(sketch, "E51.9.25", {"start": v(91.3, -52.71) * mm, "end": v(91.67, -52.88) * mm});
            skLineSegment(sketch, "E51.9.26", {"start": v(101.23, -33.02) * mm, "end": v(102.04, -33.45) * mm});
            skLineSegment(sketch, "E51.9.27", {"start": v(91.67, -52.88) * mm, "end": v(92.27, -53.14) * mm});
            skLineSegment(sketch, "E51.9.28", {"start": v(100.27, -32.58) * mm, "end": v(100.64, -32.74) * mm});
            skLineSegment(sketch, "E51.9.29", {"start": v(100.15, -32.54) * mm, "end": v(100.27, -32.58) * mm});
            skLineSegment(sketch, "E51.10.0", {"start": v(94.77, 0) * mm, "end": v(105.3, 0) * mm});
            skLineSegment(sketch, "E51.10.1", {"start": v(118.6, -19.42) * mm, "end": v(121.42, -18.33) * mm});
            skLineSegment(sketch, "E51.10.2", {"start": v(92.7, -19.7) * mm, "end": v(103, -21.9) * mm});
            skLineSegment(sketch, "E51.10.3", {"start": v(115.97, -20.28) * mm, "end": v(118.6, -19.42) * mm});
            skLineSegment(sketch, "E51.10.4", {"start": v(117.65, -4.28) * mm, "end": v(120.04, -5.67) * mm});
            skLineSegment(sketch, "E51.10.5", {"start": v(120.04, -5.67) * mm, "end": v(122.58, -7.31) * mm});
            skLineSegment(sketch, "E51.10.6", {"start": v(113.56, -20.93) * mm, "end": v(115.97, -20.28) * mm});
            skLineSegment(sketch, "E51.10.7", {"start": v(124.43, -17) * mm, "end": v(127.6, -15.4) * mm});
            skLineSegment(sketch, "E51.10.8", {"start": v(111.37, -21.41) * mm, "end": v(113.56, -20.93) * mm});
            skLineSegment(sketch, "E51.10.9", {"start": v(125.25, -9.24) * mm, "end": v(128.02, -11.46) * mm});
            skLineSegment(sketch, "E51.10.10", {"start": v(121.42, -18.33) * mm, "end": v(124.43, -17) * mm});
            skLineSegment(sketch, "E51.10.11", {"start": v(115.43, -3.13) * mm, "end": v(117.65, -4.28) * mm});
            skLineSegment(sketch, "E51.10.12", {"start": v(122.58, -7.31) * mm, "end": v(125.25, -9.24) * mm});
            skLineSegment(sketch, "E51.10.13", {"start": v(106.28, -22.03) * mm, "end": v(107.73, -21.94) * mm});
            skLineSegment(sketch, "E51.10.14", {"start": v(107.73, -21.94) * mm, "end": v(109.43, -21.74) * mm});
            skLineSegment(sketch, "E51.10.15", {"start": v(109.43, -21.74) * mm, "end": v(111.37, -21.41) * mm});
            skLineSegment(sketch, "E51.10.16", {"start": v(111.55, -1.49) * mm, "end": v(113.4, -2.21) * mm});
            skLineSegment(sketch, "E51.10.17", {"start": v(109.93, -0.94) * mm, "end": v(111.55, -1.49) * mm});
            skLineSegment(sketch, "E51.10.18", {"start": v(113.4, -2.21) * mm, "end": v(115.43, -3.13) * mm});
            skLineSegment(sketch, "E51.10.19", {"start": v(105.1, -22.05) * mm, "end": v(106.28, -22.03) * mm});
            skLineSegment(sketch, "E51.10.20", {"start": v(104.18, -22.02) * mm, "end": v(105.1, -22.05) * mm});
            skLineSegment(sketch, "E51.10.21", {"start": v(108.54, -0.55) * mm, "end": v(109.93, -0.94) * mm});
            skLineSegment(sketch, "E51.10.22", {"start": v(107.39, -0.28) * mm, "end": v(108.54, -0.55) * mm});
            skLineSegment(sketch, "E51.10.23", {"start": v(105.83, -0.04) * mm, "end": v(106.48, -0.12) * mm});
            skLineSegment(sketch, "E51.10.24", {"start": v(103, -21.9) * mm, "end": v(103.13, -21.92) * mm});
            skLineSegment(sketch, "E51.10.25", {"start": v(103.13, -21.92) * mm, "end": v(103.52, -21.97) * mm});
            skLineSegment(sketch, "E51.10.26", {"start": v(106.48, -0.12) * mm, "end": v(107.39, -0.28) * mm});
            skLineSegment(sketch, "E51.10.27", {"start": v(103.52, -21.97) * mm, "end": v(104.18, -22.02) * mm});
            skLineSegment(sketch, "E51.10.28", {"start": v(105.43, 0) * mm, "end": v(105.83, -0.04) * mm});
            skLineSegment(sketch, "E51.10.29", {"start": v(105.3, 0) * mm, "end": v(105.43, 0) * mm});
            skLineSegment(sketch, "E51.11.0", {"start": v(90.13, 29.29) * mm, "end": v(100.15, 32.54) * mm});
            skLineSegment(sketch, "E51.11.1", {"start": v(118.8, 18.18) * mm, "end": v(121.15, 20.09) * mm});
            skLineSegment(sketch, "E51.11.2", {"start": v(94.25, 9.9) * mm, "end": v(104.72, 11) * mm});
            skLineSegment(sketch, "E51.11.3", {"start": v(116.56, 16.55) * mm, "end": v(118.8, 18.18) * mm});
            skLineSegment(sketch, "E51.11.4", {"start": v(113.22, 32.29) * mm, "end": v(115.92, 31.7) * mm});
            skLineSegment(sketch, "E51.11.5", {"start": v(115.92, 31.7) * mm, "end": v(118.84, 30.93) * mm});
            skLineSegment(sketch, "E51.11.6", {"start": v(114.47, 15.18) * mm, "end": v(116.56, 16.55) * mm});
            skLineSegment(sketch, "E51.11.7", {"start": v(123.6, 22.28) * mm, "end": v(126.13, 24.78) * mm});
            skLineSegment(sketch, "E51.11.8", {"start": v(112.54, 14.05) * mm, "end": v(114.47, 15.18) * mm});
            skLineSegment(sketch, "E51.11.9", {"start": v(121.98, 29.92) * mm, "end": v(125.3, 28.66) * mm});
            skLineSegment(sketch, "E51.11.10", {"start": v(121.15, 20.09) * mm, "end": v(123.6, 22.28) * mm});
            skLineSegment(sketch, "E51.11.11", {"start": v(110.75, 32.69) * mm, "end": v(113.22, 32.29) * mm});
            skLineSegment(sketch, "E51.11.12", {"start": v(118.84, 30.93) * mm, "end": v(121.98, 29.92) * mm});
            skLineSegment(sketch, "E51.11.13", {"start": v(107.89, 11.89) * mm, "end": v(109.23, 12.43) * mm});
            skLineSegment(sketch, "E51.11.14", {"start": v(109.23, 12.43) * mm, "end": v(110.79, 13.14) * mm});
            skLineSegment(sketch, "E51.11.15", {"start": v(110.79, 13.14) * mm, "end": v(112.54, 14.05) * mm});
            skLineSegment(sketch, "E51.11.16", {"start": v(106.55, 33.06) * mm, "end": v(108.52, 32.94) * mm});
            skLineSegment(sketch, "E51.11.17", {"start": v(104.84, 33.08) * mm, "end": v(106.55, 33.06) * mm});
            skLineSegment(sketch, "E51.11.18", {"start": v(108.52, 32.94) * mm, "end": v(110.75, 32.69) * mm});
            skLineSegment(sketch, "E51.11.19", {"start": v(106.77, 11.5) * mm, "end": v(107.89, 11.89) * mm});
            skLineSegment(sketch, "E51.11.20", {"start": v(105.88, 11.25) * mm, "end": v(106.77, 11.5) * mm});
            skLineSegment(sketch, "E51.11.21", {"start": v(103.4, 33.02) * mm, "end": v(104.84, 33.08) * mm});
            skLineSegment(sketch, "E51.11.22", {"start": v(102.22, 32.92) * mm, "end": v(103.4, 33.02) * mm});
            skLineSegment(sketch, "E51.11.23", {"start": v(100.66, 32.67) * mm, "end": v(101.3, 32.8) * mm});
            skLineSegment(sketch, "E51.11.24", {"start": v(104.72, 11) * mm, "end": v(104.85, 11.03) * mm});
            skLineSegment(sketch, "E51.11.25", {"start": v(104.85, 11.03) * mm, "end": v(105.24, 11.1) * mm});
            skLineSegment(sketch, "E51.11.26", {"start": v(101.3, 32.8) * mm, "end": v(102.22, 32.92) * mm});
            skLineSegment(sketch, "E51.11.27", {"start": v(105.24, 11.1) * mm, "end": v(105.88, 11.25) * mm});
            skLineSegment(sketch, "E51.11.28", {"start": v(100.27, 32.58) * mm, "end": v(100.66, 32.67) * mm});
            skLineSegment(sketch, "E51.11.29", {"start": v(100.15, 32.54) * mm, "end": v(100.27, 32.58) * mm});
            skLineSegment(sketch, "E51.12.0", {"start": v(76.67, 55.7) * mm, "end": v(85.2, 61.9) * mm});
            skLineSegment(sketch, "E51.12.1", {"start": v(107.36, 54) * mm, "end": v(109.01, 56.54) * mm});
            skLineSegment(sketch, "E51.12.2", {"start": v(86.58, 38.55) * mm, "end": v(96.2, 42.83) * mm});
            skLineSegment(sketch, "E51.12.3", {"start": v(105.74, 51.76) * mm, "end": v(107.36, 54) * mm});
            skLineSegment(sketch, "E51.12.4", {"start": v(97.7, 65.7) * mm, "end": v(100.45, 65.98) * mm});
            skLineSegment(sketch, "E51.12.5", {"start": v(100.45, 65.98) * mm, "end": v(103.47, 66.14) * mm});
            skLineSegment(sketch, "E51.12.6", {"start": v(104.17, 49.81) * mm, "end": v(105.74, 51.76) * mm});
            skLineSegment(sketch, "E51.12.7", {"start": v(110.66, 59.38) * mm, "end": v(112.3, 62.54) * mm});
            skLineSegment(sketch, "E51.12.8", {"start": v(102.69, 48.14) * mm, "end": v(104.17, 49.81) * mm});
            skLineSegment(sketch, "E51.12.9", {"start": v(106.76, 66.15) * mm, "end": v(110.3, 65.98) * mm});
            skLineSegment(sketch, "E51.12.10", {"start": v(109.01, 56.54) * mm, "end": v(110.66, 59.38) * mm});
            skLineSegment(sketch, "E51.12.11", {"start": v(95.23, 65.31) * mm, "end": v(97.7, 65.7) * mm});
            skLineSegment(sketch, "E51.12.12", {"start": v(103.47, 66.14) * mm, "end": v(106.76, 66.15) * mm});
            skLineSegment(sketch, "E51.12.13", {"start": v(98.93, 44.65) * mm, "end": v(100.05, 45.57) * mm});
            skLineSegment(sketch, "E51.12.14", {"start": v(100.05, 45.57) * mm, "end": v(101.3, 46.73) * mm});
            skLineSegment(sketch, "E51.12.15", {"start": v(101.3, 46.73) * mm, "end": v(102.69, 48.14) * mm});
            skLineSegment(sketch, "E51.12.16", {"start": v(91.12, 64.37) * mm, "end": v(93.03, 64.86) * mm});
            skLineSegment(sketch, "E51.12.17", {"start": v(89.49, 63.86) * mm, "end": v(91.12, 64.37) * mm});
            skLineSegment(sketch, "E51.12.18", {"start": v(93.03, 64.86) * mm, "end": v(95.23, 65.31) * mm});
            skLineSegment(sketch, "E51.12.19", {"start": v(97.99, 43.93) * mm, "end": v(98.93, 44.65) * mm});
            skLineSegment(sketch, "E51.12.20", {"start": v(97.23, 43.42) * mm, "end": v(97.99, 43.93) * mm});
            skLineSegment(sketch, "E51.12.21", {"start": v(88.13, 63.36) * mm, "end": v(89.49, 63.86) * mm});
            skLineSegment(sketch, "E51.12.22", {"start": v(87.04, 62.9) * mm, "end": v(88.13, 63.36) * mm});
            skLineSegment(sketch, "E51.12.23", {"start": v(85.64, 62.17) * mm, "end": v(86.21, 62.5) * mm});
            skLineSegment(sketch, "E51.12.24", {"start": v(96.2, 42.83) * mm, "end": v(96.32, 42.89) * mm});
            skLineSegment(sketch, "E51.12.25", {"start": v(96.32, 42.89) * mm, "end": v(96.66, 43.08) * mm});
            skLineSegment(sketch, "E51.12.26", {"start": v(86.21, 62.5) * mm, "end": v(87.04, 62.9) * mm});
            skLineSegment(sketch, "E51.12.27", {"start": v(96.66, 43.08) * mm, "end": v(97.23, 43.42) * mm});
            skLineSegment(sketch, "E51.12.28", {"start": v(85.3, 61.97) * mm, "end": v(85.64, 62.17) * mm});
            skLineSegment(sketch, "E51.12.29", {"start": v(85.2, 61.9) * mm, "end": v(85.3, 61.97) * mm});
            skLineSegment(sketch, "E51.13.0", {"start": v(55.7, 76.67) * mm, "end": v(61.9, 85.2) * mm});
            skLineSegment(sketch, "E51.13.1", {"start": v(85.42, 84.53) * mm, "end": v(86.2, 87.46) * mm});
            skLineSegment(sketch, "E51.13.2", {"start": v(70.43, 63.41) * mm, "end": v(78.25, 70.46) * mm});
            skLineSegment(sketch, "E51.13.3", {"start": v(84.57, 81.9) * mm, "end": v(85.42, 84.53) * mm});
            skLineSegment(sketch, "E51.13.4", {"start": v(72.62, 92.67) * mm, "end": v(75.14, 93.79) * mm});
            skLineSegment(sketch, "E51.13.5", {"start": v(75.14, 93.79) * mm, "end": v(77.97, 94.87) * mm});
            skLineSegment(sketch, "E51.13.6", {"start": v(83.68, 79.57) * mm, "end": v(84.57, 81.9) * mm});
            skLineSegment(sketch, "E51.13.7", {"start": v(86.9, 90.67) * mm, "end": v(87.47, 94.18) * mm});
            skLineSegment(sketch, "E51.13.8", {"start": v(82.79, 77.52) * mm, "end": v(83.68, 79.57) * mm});
            skLineSegment(sketch, "E51.13.9", {"start": v(81.1, 95.9) * mm, "end": v(84.52, 96.84) * mm});
            skLineSegment(sketch, "E51.13.10", {"start": v(86.2, 87.46) * mm, "end": v(86.9, 90.67) * mm});
            skLineSegment(sketch, "E51.13.11", {"start": v(70.38, 91.54) * mm, "end": v(72.62, 92.67) * mm});
            skLineSegment(sketch, "E51.13.12", {"start": v(77.97, 94.87) * mm, "end": v(81.1, 95.9) * mm});
            skLineSegment(sketch, "E51.13.13", {"start": v(80.3, 73.03) * mm, "end": v(81.07, 74.26) * mm});
            skLineSegment(sketch, "E51.13.14", {"start": v(81.07, 74.26) * mm, "end": v(81.9, 75.75) * mm});
            skLineSegment(sketch, "E51.13.15", {"start": v(81.9, 75.75) * mm, "end": v(82.79, 77.52) * mm});
            skLineSegment(sketch, "E51.13.16", {"start": v(66.77, 89.38) * mm, "end": v(68.44, 90.44) * mm});
            skLineSegment(sketch, "E51.13.17", {"start": v(65.38, 88.39) * mm, "end": v(66.77, 89.38) * mm});
            skLineSegment(sketch, "E51.13.18", {"start": v(68.44, 90.44) * mm, "end": v(70.38, 91.54) * mm});
            skLineSegment(sketch, "E51.13.19", {"start": v(79.62, 72.06) * mm, "end": v(80.3, 73.03) * mm});
            skLineSegment(sketch, "E51.13.20", {"start": v(79.05, 71.34) * mm, "end": v(79.62, 72.06) * mm});
            skLineSegment(sketch, "E51.13.21", {"start": v(64.24, 87.5) * mm, "end": v(65.38, 88.39) * mm});
            skLineSegment(sketch, "E51.13.22", {"start": v(63.35, 86.71) * mm, "end": v(64.24, 87.5) * mm});
            skLineSegment(sketch, "E51.13.23", {"start": v(62.23, 85.6) * mm, "end": v(62.68, 86.07) * mm});
            skLineSegment(sketch, "E51.13.24", {"start": v(78.25, 70.46) * mm, "end": v(78.35, 70.55) * mm});
            skLineSegment(sketch, "E51.13.25", {"start": v(78.35, 70.55) * mm, "end": v(78.62, 70.84) * mm});
            skLineSegment(sketch, "E51.13.26", {"start": v(62.68, 86.07) * mm, "end": v(63.35, 86.71) * mm});
            skLineSegment(sketch, "E51.13.27", {"start": v(78.62, 70.84) * mm, "end": v(79.05, 71.34) * mm});
            skLineSegment(sketch, "E51.13.28", {"start": v(61.98, 85.3) * mm, "end": v(62.23, 85.6) * mm});
            skLineSegment(sketch, "E51.13.29", {"start": v(61.9, 85.2) * mm, "end": v(61.98, 85.3) * mm});
            skLineSegment(sketch, "E51.14.0", {"start": v(29.29, 90.13) * mm, "end": v(32.54, 100.15) * mm});
            skLineSegment(sketch, "E51.14.1", {"start": v(55.12, 106.8) * mm, "end": v(54.96, 109.82) * mm});
            skLineSegment(sketch, "E51.14.2", {"start": v(47.39, 82.07) * mm, "end": v(52.65, 91.2) * mm});
            skLineSegment(sketch, "E51.14.3", {"start": v(55.12, 104.03) * mm, "end": v(55.12, 106.8) * mm});
            skLineSegment(sketch, "E51.14.4", {"start": v(40.43, 110.57) * mm, "end": v(42.48, 112.42) * mm});
            skLineSegment(sketch, "E51.14.5", {"start": v(42.48, 112.42) * mm, "end": v(44.83, 114.32) * mm});
            skLineSegment(sketch, "E51.14.6", {"start": v(55, 101.53) * mm, "end": v(55.12, 104.03) * mm});
            skLineSegment(sketch, "E51.14.7", {"start": v(54.62, 113.09) * mm, "end": v(54.09, 116.6) * mm});
            skLineSegment(sketch, "E51.14.8", {"start": v(54.78, 99.3) * mm, "end": v(55, 101.53) * mm});
            skLineSegment(sketch, "E51.14.9", {"start": v(47.5, 116.27) * mm, "end": v(50.46, 118.22) * mm});
            skLineSegment(sketch, "E51.14.10", {"start": v(54.96, 109.82) * mm, "end": v(54.62, 113.09) * mm});
            skLineSegment(sketch, "E51.14.11", {"start": v(38.65, 108.81) * mm, "end": v(40.43, 110.57) * mm});
            skLineSegment(sketch, "E51.14.12", {"start": v(44.83, 114.32) * mm, "end": v(47.5, 116.27) * mm});
            skLineSegment(sketch, "E51.14.13", {"start": v(53.8, 94.27) * mm, "end": v(54.15, 95.67) * mm});
            skLineSegment(sketch, "E51.14.14", {"start": v(54.15, 95.67) * mm, "end": v(54.49, 97.35) * mm});
            skLineSegment(sketch, "E51.14.15", {"start": v(54.49, 97.35) * mm, "end": v(54.78, 99.3) * mm});
            skLineSegment(sketch, "E51.14.16", {"start": v(35.89, 105.64) * mm, "end": v(37.14, 107.16) * mm});
            skLineSegment(sketch, "E51.14.17", {"start": v(34.86, 104.26) * mm, "end": v(35.89, 105.64) * mm});
            skLineSegment(sketch, "E51.14.18", {"start": v(37.14, 107.16) * mm, "end": v(38.65, 108.81) * mm});
            skLineSegment(sketch, "E51.14.19", {"start": v(53.45, 93.14) * mm, "end": v(53.8, 94.27) * mm});
            skLineSegment(sketch, "E51.14.20", {"start": v(53.14, 92.27) * mm, "end": v(53.45, 93.14) * mm});
            skLineSegment(sketch, "E51.14.21", {"start": v(34.06, 103.06) * mm, "end": v(34.86, 104.26) * mm});
            skLineSegment(sketch, "E51.14.22", {"start": v(33.45, 102.04) * mm, "end": v(34.06, 103.06) * mm});
            skLineSegment(sketch, "E51.14.23", {"start": v(32.74, 100.64) * mm, "end": v(33.02, 101.23) * mm});
            skLineSegment(sketch, "E51.14.24", {"start": v(52.65, 91.2) * mm, "end": v(52.71, 91.3) * mm});
            skLineSegment(sketch, "E51.14.25", {"start": v(52.71, 91.3) * mm, "end": v(52.88, 91.67) * mm});
            skLineSegment(sketch, "E51.14.26", {"start": v(33.02, 101.23) * mm, "end": v(33.45, 102.04) * mm});
            skLineSegment(sketch, "E51.14.27", {"start": v(52.88, 91.67) * mm, "end": v(53.14, 92.27) * mm});
            skLineSegment(sketch, "E51.14.28", {"start": v(32.58, 100.27) * mm, "end": v(32.74, 100.64) * mm});
            skLineSegment(sketch, "E51.14.29", {"start": v(32.54, 100.15) * mm, "end": v(32.58, 100.27) * mm});
            skLineSegment(sketch, "E51.15.0", {"start": v(0, 94.77) * mm, "end": v(0, 105.3) * mm});
            skLineSegment(sketch, "E51.15.1", {"start": v(19.42, 118.6) * mm, "end": v(18.33, 121.42) * mm});
            skLineSegment(sketch, "E51.15.2", {"start": v(19.7, 92.7) * mm, "end": v(21.9, 103) * mm});
            skLineSegment(sketch, "E51.15.3", {"start": v(20.28, 115.97) * mm, "end": v(19.42, 118.6) * mm});
            skLineSegment(sketch, "E51.15.4", {"start": v(4.28, 117.65) * mm, "end": v(5.67, 120.04) * mm});
            skLineSegment(sketch, "E51.15.5", {"start": v(5.67, 120.04) * mm, "end": v(7.31, 122.58) * mm});
            skLineSegment(sketch, "E51.15.6", {"start": v(20.93, 113.56) * mm, "end": v(20.28, 115.97) * mm});
            skLineSegment(sketch, "E51.15.7", {"start": v(17, 124.43) * mm, "end": v(15.4, 127.6) * mm});
            skLineSegment(sketch, "E51.15.8", {"start": v(21.41, 111.37) * mm, "end": v(20.93, 113.56) * mm});
            skLineSegment(sketch, "E51.15.9", {"start": v(9.24, 125.25) * mm, "end": v(11.46, 128.02) * mm});
            skLineSegment(sketch, "E51.15.10", {"start": v(18.33, 121.42) * mm, "end": v(17, 124.43) * mm});
            skLineSegment(sketch, "E51.15.11", {"start": v(3.13, 115.43) * mm, "end": v(4.28, 117.65) * mm});
            skLineSegment(sketch, "E51.15.12", {"start": v(7.31, 122.58) * mm, "end": v(9.24, 125.25) * mm});
            skLineSegment(sketch, "E51.15.13", {"start": v(22.03, 106.28) * mm, "end": v(21.94, 107.73) * mm});
            skLineSegment(sketch, "E51.15.14", {"start": v(21.94, 107.73) * mm, "end": v(21.74, 109.43) * mm});
            skLineSegment(sketch, "E51.15.15", {"start": v(21.74, 109.43) * mm, "end": v(21.41, 111.37) * mm});
            skLineSegment(sketch, "E51.15.16", {"start": v(1.49, 111.55) * mm, "end": v(2.21, 113.4) * mm});
            skLineSegment(sketch, "E51.15.17", {"start": v(0.94, 109.93) * mm, "end": v(1.49, 111.55) * mm});
            skLineSegment(sketch, "E51.15.18", {"start": v(2.21, 113.4) * mm, "end": v(3.13, 115.43) * mm});
            skLineSegment(sketch, "E51.15.19", {"start": v(22.05, 105.1) * mm, "end": v(22.03, 106.28) * mm});
            skLineSegment(sketch, "E51.15.20", {"start": v(22.02, 104.18) * mm, "end": v(22.05, 105.1) * mm});
            skLineSegment(sketch, "E51.15.21", {"start": v(0.55, 108.54) * mm, "end": v(0.94, 109.93) * mm});
            skLineSegment(sketch, "E51.15.22", {"start": v(0.28, 107.39) * mm, "end": v(0.55, 108.54) * mm});
            skLineSegment(sketch, "E51.15.23", {"start": v(0.04, 105.83) * mm, "end": v(0.12, 106.48) * mm});
            skLineSegment(sketch, "E51.15.24", {"start": v(21.9, 103) * mm, "end": v(21.92, 103.13) * mm});
            skLineSegment(sketch, "E51.15.25", {"start": v(21.92, 103.13) * mm, "end": v(21.97, 103.52) * mm});
            skLineSegment(sketch, "E51.15.26", {"start": v(0.12, 106.48) * mm, "end": v(0.28, 107.39) * mm});
            skLineSegment(sketch, "E51.15.27", {"start": v(21.97, 103.52) * mm, "end": v(22.02, 104.18) * mm});
            skLineSegment(sketch, "E51.15.28", {"start": v(0, 105.43) * mm, "end": v(0.04, 105.83) * mm});
            skLineSegment(sketch, "E51.15.29", {"start": v(0, 105.3) * mm, "end": v(0, 105.43) * mm});
            skLineSegment(sketch, "E51.16.0", {"start": v(-29.29, 90.13) * mm, "end": v(-32.54, 100.15) * mm});
            skLineSegment(sketch, "E51.16.1", {"start": v(-18.18, 118.8) * mm, "end": v(-20.09, 121.15) * mm});
            skLineSegment(sketch, "E51.16.2", {"start": v(-9.9, 94.25) * mm, "end": v(-11, 104.72) * mm});
            skLineSegment(sketch, "E51.16.3", {"start": v(-16.55, 116.56) * mm, "end": v(-18.18, 118.8) * mm});
            skLineSegment(sketch, "E51.16.4", {"start": v(-32.29, 113.22) * mm, "end": v(-31.7, 115.92) * mm});
            skLineSegment(sketch, "E51.16.5", {"start": v(-31.7, 115.92) * mm, "end": v(-30.93, 118.84) * mm});
            skLineSegment(sketch, "E51.16.6", {"start": v(-15.18, 114.47) * mm, "end": v(-16.55, 116.56) * mm});
            skLineSegment(sketch, "E51.16.7", {"start": v(-22.28, 123.6) * mm, "end": v(-24.78, 126.13) * mm});
            skLineSegment(sketch, "E51.16.8", {"start": v(-14.05, 112.54) * mm, "end": v(-15.18, 114.47) * mm});
            skLineSegment(sketch, "E51.16.9", {"start": v(-29.92, 121.98) * mm, "end": v(-28.66, 125.3) * mm});
            skLineSegment(sketch, "E51.16.10", {"start": v(-20.09, 121.15) * mm, "end": v(-22.28, 123.6) * mm});
            skLineSegment(sketch, "E51.16.11", {"start": v(-32.69, 110.75) * mm, "end": v(-32.29, 113.22) * mm});
            skLineSegment(sketch, "E51.16.12", {"start": v(-30.93, 118.84) * mm, "end": v(-29.92, 121.98) * mm});
            skLineSegment(sketch, "E51.16.13", {"start": v(-11.89, 107.89) * mm, "end": v(-12.43, 109.23) * mm});
            skLineSegment(sketch, "E51.16.14", {"start": v(-12.43, 109.23) * mm, "end": v(-13.14, 110.79) * mm});
            skLineSegment(sketch, "E51.16.15", {"start": v(-13.14, 110.79) * mm, "end": v(-14.05, 112.54) * mm});
            skLineSegment(sketch, "E51.16.16", {"start": v(-33.06, 106.55) * mm, "end": v(-32.94, 108.52) * mm});
            skLineSegment(sketch, "E51.16.17", {"start": v(-33.08, 104.84) * mm, "end": v(-33.06, 106.55) * mm});
            skLineSegment(sketch, "E51.16.18", {"start": v(-32.94, 108.52) * mm, "end": v(-32.69, 110.75) * mm});
            skLineSegment(sketch, "E51.16.19", {"start": v(-11.5, 106.77) * mm, "end": v(-11.89, 107.89) * mm});
            skLineSegment(sketch, "E51.16.20", {"start": v(-11.25, 105.88) * mm, "end": v(-11.5, 106.77) * mm});
            skLineSegment(sketch, "E51.16.21", {"start": v(-33.02, 103.4) * mm, "end": v(-33.08, 104.84) * mm});
            skLineSegment(sketch, "E51.16.22", {"start": v(-32.92, 102.22) * mm, "end": v(-33.02, 103.4) * mm});
            skLineSegment(sketch, "E51.16.23", {"start": v(-32.67, 100.66) * mm, "end": v(-32.8, 101.3) * mm});
            skLineSegment(sketch, "E51.16.24", {"start": v(-11, 104.72) * mm, "end": v(-11.03, 104.85) * mm});
            skLineSegment(sketch, "E51.16.25", {"start": v(-11.03, 104.85) * mm, "end": v(-11.1, 105.24) * mm});
            skLineSegment(sketch, "E51.16.26", {"start": v(-32.8, 101.3) * mm, "end": v(-32.92, 102.22) * mm});
            skLineSegment(sketch, "E51.16.27", {"start": v(-11.1, 105.24) * mm, "end": v(-11.25, 105.88) * mm});
            skLineSegment(sketch, "E51.16.28", {"start": v(-32.58, 100.27) * mm, "end": v(-32.67, 100.66) * mm});
            skLineSegment(sketch, "E51.16.29", {"start": v(-32.54, 100.15) * mm, "end": v(-32.58, 100.27) * mm});
            skLineSegment(sketch, "E51.17.0", {"start": v(-55.7, 76.67) * mm, "end": v(-61.9, 85.2) * mm});
            skLineSegment(sketch, "E51.17.1", {"start": v(-54, 107.36) * mm, "end": v(-56.54, 109.01) * mm});
            skLineSegment(sketch, "E51.17.2", {"start": v(-38.55, 86.58) * mm, "end": v(-42.83, 96.2) * mm});
            skLineSegment(sketch, "E51.17.3", {"start": v(-51.76, 105.74) * mm, "end": v(-54, 107.36) * mm});
            skLineSegment(sketch, "E51.17.4", {"start": v(-65.7, 97.7) * mm, "end": v(-65.98, 100.45) * mm});
            skLineSegment(sketch, "E51.17.5", {"start": v(-65.98, 100.45) * mm, "end": v(-66.14, 103.47) * mm});
            skLineSegment(sketch, "E51.17.6", {"start": v(-49.81, 104.17) * mm, "end": v(-51.76, 105.74) * mm});
            skLineSegment(sketch, "E51.17.7", {"start": v(-59.38, 110.66) * mm, "end": v(-62.54, 112.3) * mm});
            skLineSegment(sketch, "E51.17.8", {"start": v(-48.14, 102.69) * mm, "end": v(-49.81, 104.17) * mm});
            skLineSegment(sketch, "E51.17.9", {"start": v(-66.15, 106.76) * mm, "end": v(-65.98, 110.3) * mm});
            skLineSegment(sketch, "E51.17.10", {"start": v(-56.54, 109.01) * mm, "end": v(-59.38, 110.66) * mm});
            skLineSegment(sketch, "E51.17.11", {"start": v(-65.31, 95.23) * mm, "end": v(-65.7, 97.7) * mm});
            skLineSegment(sketch, "E51.17.12", {"start": v(-66.14, 103.47) * mm, "end": v(-66.15, 106.76) * mm});
            skLineSegment(sketch, "E51.17.13", {"start": v(-44.65, 98.93) * mm, "end": v(-45.57, 100.05) * mm});
            skLineSegment(sketch, "E51.17.14", {"start": v(-45.57, 100.05) * mm, "end": v(-46.73, 101.3) * mm});
            skLineSegment(sketch, "E51.17.15", {"start": v(-46.73, 101.3) * mm, "end": v(-48.14, 102.69) * mm});
            skLineSegment(sketch, "E51.17.16", {"start": v(-64.37, 91.12) * mm, "end": v(-64.86, 93.03) * mm});
            skLineSegment(sketch, "E51.17.17", {"start": v(-63.86, 89.49) * mm, "end": v(-64.37, 91.12) * mm});
            skLineSegment(sketch, "E51.17.18", {"start": v(-64.86, 93.03) * mm, "end": v(-65.31, 95.23) * mm});
            skLineSegment(sketch, "E51.17.19", {"start": v(-43.93, 97.99) * mm, "end": v(-44.65, 98.93) * mm});
            skLineSegment(sketch, "E51.17.20", {"start": v(-43.42, 97.23) * mm, "end": v(-43.93, 97.99) * mm});
            skLineSegment(sketch, "E51.17.21", {"start": v(-63.36, 88.13) * mm, "end": v(-63.86, 89.49) * mm});
            skLineSegment(sketch, "E51.17.22", {"start": v(-62.9, 87.04) * mm, "end": v(-63.36, 88.13) * mm});
            skLineSegment(sketch, "E51.17.23", {"start": v(-62.17, 85.64) * mm, "end": v(-62.5, 86.21) * mm});
            skLineSegment(sketch, "E51.17.24", {"start": v(-42.83, 96.2) * mm, "end": v(-42.89, 96.32) * mm});
            skLineSegment(sketch, "E51.17.25", {"start": v(-42.89, 96.32) * mm, "end": v(-43.08, 96.66) * mm});
            skLineSegment(sketch, "E51.17.26", {"start": v(-62.5, 86.21) * mm, "end": v(-62.9, 87.04) * mm});
            skLineSegment(sketch, "E51.17.27", {"start": v(-43.08, 96.66) * mm, "end": v(-43.42, 97.23) * mm});
            skLineSegment(sketch, "E51.17.28", {"start": v(-61.97, 85.3) * mm, "end": v(-62.17, 85.64) * mm});
            skLineSegment(sketch, "E51.17.29", {"start": v(-61.9, 85.2) * mm, "end": v(-61.97, 85.3) * mm});
            skLineSegment(sketch, "E51.18.0", {"start": v(-76.67, 55.7) * mm, "end": v(-85.2, 61.9) * mm});
            skLineSegment(sketch, "E51.18.1", {"start": v(-84.53, 85.42) * mm, "end": v(-87.46, 86.2) * mm});
            skLineSegment(sketch, "E51.18.2", {"start": v(-63.41, 70.43) * mm, "end": v(-70.46, 78.25) * mm});
            skLineSegment(sketch, "E51.18.3", {"start": v(-81.9, 84.57) * mm, "end": v(-84.53, 85.42) * mm});
            skLineSegment(sketch, "E51.18.4", {"start": v(-92.67, 72.62) * mm, "end": v(-93.79, 75.14) * mm});
            skLineSegment(sketch, "E51.18.5", {"start": v(-93.79, 75.14) * mm, "end": v(-94.87, 77.97) * mm});
            skLineSegment(sketch, "E51.18.6", {"start": v(-79.57, 83.68) * mm, "end": v(-81.9, 84.57) * mm});
            skLineSegment(sketch, "E51.18.7", {"start": v(-90.67, 86.9) * mm, "end": v(-94.18, 87.47) * mm});
            skLineSegment(sketch, "E51.18.8", {"start": v(-77.52, 82.79) * mm, "end": v(-79.57, 83.68) * mm});
            skLineSegment(sketch, "E51.18.9", {"start": v(-95.9, 81.1) * mm, "end": v(-96.84, 84.52) * mm});
            skLineSegment(sketch, "E51.18.10", {"start": v(-87.46, 86.2) * mm, "end": v(-90.67, 86.9) * mm});
            skLineSegment(sketch, "E51.18.11", {"start": v(-91.54, 70.38) * mm, "end": v(-92.67, 72.62) * mm});
            skLineSegment(sketch, "E51.18.12", {"start": v(-94.87, 77.97) * mm, "end": v(-95.9, 81.1) * mm});
            skLineSegment(sketch, "E51.18.13", {"start": v(-73.03, 80.3) * mm, "end": v(-74.26, 81.07) * mm});
            skLineSegment(sketch, "E51.18.14", {"start": v(-74.26, 81.07) * mm, "end": v(-75.75, 81.9) * mm});
            skLineSegment(sketch, "E51.18.15", {"start": v(-75.75, 81.9) * mm, "end": v(-77.52, 82.79) * mm});
            skLineSegment(sketch, "E51.18.16", {"start": v(-89.38, 66.77) * mm, "end": v(-90.44, 68.44) * mm});
            skLineSegment(sketch, "E51.18.17", {"start": v(-88.39, 65.38) * mm, "end": v(-89.38, 66.77) * mm});
            skLineSegment(sketch, "E51.18.18", {"start": v(-90.44, 68.44) * mm, "end": v(-91.54, 70.38) * mm});
            skLineSegment(sketch, "E51.18.19", {"start": v(-72.06, 79.62) * mm, "end": v(-73.03, 80.3) * mm});
            skLineSegment(sketch, "E51.18.20", {"start": v(-71.34, 79.05) * mm, "end": v(-72.06, 79.62) * mm});
            skLineSegment(sketch, "E51.18.21", {"start": v(-87.5, 64.24) * mm, "end": v(-88.39, 65.38) * mm});
            skLineSegment(sketch, "E51.18.22", {"start": v(-86.71, 63.35) * mm, "end": v(-87.5, 64.24) * mm});
            skLineSegment(sketch, "E51.18.23", {"start": v(-85.6, 62.23) * mm, "end": v(-86.07, 62.68) * mm});
            skLineSegment(sketch, "E51.18.24", {"start": v(-70.46, 78.25) * mm, "end": v(-70.55, 78.35) * mm});
            skLineSegment(sketch, "E51.18.25", {"start": v(-70.55, 78.35) * mm, "end": v(-70.84, 78.62) * mm});
            skLineSegment(sketch, "E51.18.26", {"start": v(-86.07, 62.68) * mm, "end": v(-86.71, 63.35) * mm});
            skLineSegment(sketch, "E51.18.27", {"start": v(-70.84, 78.62) * mm, "end": v(-71.34, 79.05) * mm});
            skLineSegment(sketch, "E51.18.28", {"start": v(-85.3, 61.98) * mm, "end": v(-85.6, 62.23) * mm});
            skLineSegment(sketch, "E51.18.29", {"start": v(-85.2, 61.9) * mm, "end": v(-85.3, 61.98) * mm});
            skLineSegment(sketch, "E51.19.0", {"start": v(-90.13, 29.29) * mm, "end": v(-100.15, 32.54) * mm});
            skLineSegment(sketch, "E51.19.1", {"start": v(-106.8, 55.12) * mm, "end": v(-109.82, 54.96) * mm});
            skLineSegment(sketch, "E51.19.2", {"start": v(-82.07, 47.39) * mm, "end": v(-91.2, 52.65) * mm});
            skLineSegment(sketch, "E51.19.3", {"start": v(-104.03, 55.12) * mm, "end": v(-106.8, 55.12) * mm});
            skLineSegment(sketch, "E51.19.4", {"start": v(-110.57, 40.43) * mm, "end": v(-112.42, 42.48) * mm});
            skLineSegment(sketch, "E51.19.5", {"start": v(-112.42, 42.48) * mm, "end": v(-114.32, 44.83) * mm});
            skLineSegment(sketch, "E51.19.6", {"start": v(-101.53, 55) * mm, "end": v(-104.03, 55.12) * mm});
            skLineSegment(sketch, "E51.19.7", {"start": v(-113.09, 54.62) * mm, "end": v(-116.6, 54.09) * mm});
            skLineSegment(sketch, "E51.19.8", {"start": v(-99.3, 54.78) * mm, "end": v(-101.53, 55) * mm});
            skLineSegment(sketch, "E51.19.9", {"start": v(-116.27, 47.5) * mm, "end": v(-118.22, 50.46) * mm});
            skLineSegment(sketch, "E51.19.10", {"start": v(-109.82, 54.96) * mm, "end": v(-113.09, 54.62) * mm});
            skLineSegment(sketch, "E51.19.11", {"start": v(-108.81, 38.65) * mm, "end": v(-110.57, 40.43) * mm});
            skLineSegment(sketch, "E51.19.12", {"start": v(-114.32, 44.83) * mm, "end": v(-116.27, 47.5) * mm});
            skLineSegment(sketch, "E51.19.13", {"start": v(-94.27, 53.8) * mm, "end": v(-95.67, 54.15) * mm});
            skLineSegment(sketch, "E51.19.14", {"start": v(-95.67, 54.15) * mm, "end": v(-97.35, 54.49) * mm});
            skLineSegment(sketch, "E51.19.15", {"start": v(-97.35, 54.49) * mm, "end": v(-99.3, 54.78) * mm});
            skLineSegment(sketch, "E51.19.16", {"start": v(-105.64, 35.89) * mm, "end": v(-107.16, 37.14) * mm});
            skLineSegment(sketch, "E51.19.17", {"start": v(-104.26, 34.86) * mm, "end": v(-105.64, 35.89) * mm});
            skLineSegment(sketch, "E51.19.18", {"start": v(-107.16, 37.14) * mm, "end": v(-108.81, 38.65) * mm});
            skLineSegment(sketch, "E51.19.19", {"start": v(-93.14, 53.45) * mm, "end": v(-94.27, 53.8) * mm});
            skLineSegment(sketch, "E51.19.20", {"start": v(-92.27, 53.14) * mm, "end": v(-93.14, 53.45) * mm});
            skLineSegment(sketch, "E51.19.21", {"start": v(-103.06, 34.06) * mm, "end": v(-104.26, 34.86) * mm});
            skLineSegment(sketch, "E51.19.22", {"start": v(-102.04, 33.45) * mm, "end": v(-103.06, 34.06) * mm});
            skLineSegment(sketch, "E51.19.23", {"start": v(-100.64, 32.74) * mm, "end": v(-101.23, 33.02) * mm});
            skLineSegment(sketch, "E51.19.24", {"start": v(-91.2, 52.65) * mm, "end": v(-91.3, 52.71) * mm});
            skLineSegment(sketch, "E51.19.25", {"start": v(-91.3, 52.71) * mm, "end": v(-91.67, 52.88) * mm});
            skLineSegment(sketch, "E51.19.26", {"start": v(-101.23, 33.02) * mm, "end": v(-102.04, 33.45) * mm});
            skLineSegment(sketch, "E51.19.27", {"start": v(-91.67, 52.88) * mm, "end": v(-92.27, 53.14) * mm});
            skLineSegment(sketch, "E51.19.28", {"start": v(-100.27, 32.58) * mm, "end": v(-100.64, 32.74) * mm});
            skLineSegment(sketch, "E51.19.29", {"start": v(-100.15, 32.54) * mm, "end": v(-100.27, 32.58) * mm});
            skSolve(sketch);
        }
        {
            var Q0;
            {var subQ0=sQuery(id+"F1.wireOp",EDGE,"E0");var subQ27=makeQuery(id+"F1.imprint","INTERSECT",VERTEX,{"derivedFrom":[subQ0,sQuery(id+"F1.wireOp",EDGE,"E51.10.0")]});Q0=makeQuery(id+"F1.imprint","IMPRINT",FACE,{"disambiguationData":[TD([[makeQuery(id+"F1.imprint","IMPRINT",EDGE,{"disambiguationData":[TD([[subQ27,-1.0]])],"derivedFrom":subQ0}),1.0]])]});}
            var Q1;
            {var subQ0=sQuery(id+"F1.wireOp",EDGE,"E51.1.0");Q1=makeQuery(id+"F1.imprint","IMPRINT",FACE,{"disambiguationData":[TD([[makeQuery(id+"F1.imprint","IMPRINT",EDGE,{"derivedFrom":subQ0}),-1.0]])]});}
            var Q2;
            {var subQ7=sQuery(id+"F1.wireOp",EDGE,"E51.2.0");Q2=makeQuery(id+"F1.imprint","IMPRINT",FACE,{"disambiguationData":[TD([[makeQuery(id+"F1.imprint","IMPRINT",EDGE,{"derivedFrom":subQ7}),-1.0]])]});}
            var Q3;
            {var subQ8=sQuery(id+"F1.wireOp",EDGE,"E51.3.0");Q3=makeQuery(id+"F1.imprint","IMPRINT",FACE,{"disambiguationData":[TD([[makeQuery(id+"F1.imprint","IMPRINT",EDGE,{"derivedFrom":subQ8}),-1.0]])]});}
            var Q4;
            {var subQ2=sQuery(id+"F1.wireOp",EDGE,"E51.4.0");Q4=makeQuery(id+"F1.imprint","IMPRINT",FACE,{"disambiguationData":[TD([[makeQuery(id+"F1.imprint","IMPRINT",EDGE,{"derivedFrom":subQ2}),-1.0]])]});}
            var Q5;
            {var subQ8=sQuery(id+"F1.wireOp",EDGE,"E51.5.0");Q5=makeQuery(id+"F1.imprint","IMPRINT",FACE,{"disambiguationData":[TD([[makeQuery(id+"F1.imprint","IMPRINT",EDGE,{"derivedFrom":subQ8}),-1.0]])]});}
            var Q6;
            {var subQ3=sQuery(id+"F1.wireOp",EDGE,"E51.6.0");Q6=makeQuery(id+"F1.imprint","IMPRINT",FACE,{"disambiguationData":[TD([[makeQuery(id+"F1.imprint","IMPRINT",EDGE,{"derivedFrom":subQ3}),-1.0]])]});}
            var Q7;
            {var subQ0=sQuery(id+"F1.wireOp",EDGE,"E51.7.0");Q7=makeQuery(id+"F1.imprint","IMPRINT",FACE,{"disambiguationData":[TD([[makeQuery(id+"F1.imprint","IMPRINT",EDGE,{"derivedFrom":subQ0}),-1.0]])]});}
            var Q8;
            {var subQ5=sQuery(id+"F1.wireOp",EDGE,"E51.8.0");Q8=makeQuery(id+"F1.imprint","IMPRINT",FACE,{"disambiguationData":[TD([[makeQuery(id+"F1.imprint","IMPRINT",EDGE,{"derivedFrom":subQ5}),-1.0]])]});}
            var Q9;
            {var subQ1=sQuery(id+"F1.wireOp",EDGE,"E51.9.0");Q9=makeQuery(id+"F1.imprint","IMPRINT",FACE,{"disambiguationData":[TD([[makeQuery(id+"F1.imprint","IMPRINT",EDGE,{"derivedFrom":subQ1}),-1.0]])]});}
            var Q10;
            {var subQ5=sQuery(id+"F1.wireOp",EDGE,"E51.10.0");Q10=makeQuery(id+"F1.imprint","IMPRINT",FACE,{"disambiguationData":[TD([[makeQuery(id+"F1.imprint","IMPRINT",EDGE,{"derivedFrom":subQ5}),-1.0]])]});}
            var Q11;
            {var subQ8=sQuery(id+"F1.wireOp",EDGE,"E51.11.0");Q11=makeQuery(id+"F1.imprint","IMPRINT",FACE,{"disambiguationData":[TD([[makeQuery(id+"F1.imprint","IMPRINT",EDGE,{"derivedFrom":subQ8}),-1.0]])]});}
            var Q12;
            {var subQ2=sQuery(id+"F1.wireOp",EDGE,"E51.12.0");Q12=makeQuery(id+"F1.imprint","IMPRINT",FACE,{"disambiguationData":[TD([[makeQuery(id+"F1.imprint","IMPRINT",EDGE,{"derivedFrom":subQ2}),-1.0]])]});}
            var Q13;
            {var subQ3=sQuery(id+"F1.wireOp",EDGE,"E51.13.0");Q13=makeQuery(id+"F1.imprint","IMPRINT",FACE,{"disambiguationData":[TD([[makeQuery(id+"F1.imprint","IMPRINT",EDGE,{"derivedFrom":subQ3}),-1.0]])]});}
            var Q14;
            {var subQ0=sQuery(id+"F1.wireOp",EDGE,"E51.14.0");Q14=makeQuery(id+"F1.imprint","IMPRINT",FACE,{"disambiguationData":[TD([[makeQuery(id+"F1.imprint","IMPRINT",EDGE,{"derivedFrom":subQ0}),-1.0]])]});}
            var Q15;
            {var subQ6=sQuery(id+"F1.wireOp",EDGE,"E51.15.0");Q15=makeQuery(id+"F1.imprint","IMPRINT",FACE,{"disambiguationData":[TD([[makeQuery(id+"F1.imprint","IMPRINT",EDGE,{"derivedFrom":subQ6}),-1.0]])]});}
            var Q16;
            {var subQ5=sQuery(id+"F1.wireOp",EDGE,"E51.16.0");Q16=makeQuery(id+"F1.imprint","IMPRINT",FACE,{"disambiguationData":[TD([[makeQuery(id+"F1.imprint","IMPRINT",EDGE,{"derivedFrom":subQ5}),-1.0]])]});}
            var Q17;
            {var subQ7=sQuery(id+"F1.wireOp",EDGE,"E51.17.0");Q17=makeQuery(id+"F1.imprint","IMPRINT",FACE,{"disambiguationData":[TD([[makeQuery(id+"F1.imprint","IMPRINT",EDGE,{"derivedFrom":subQ7}),-1.0]])]});}
            var Q18;
            {var subQ5=sQuery(id+"F1.wireOp",EDGE,"E51.18.0");Q18=makeQuery(id+"F1.imprint","IMPRINT",FACE,{"disambiguationData":[TD([[makeQuery(id+"F1.imprint","IMPRINT",EDGE,{"derivedFrom":subQ5}),-1.0]])]});}
            var Q19;
            {var subQ8=sQuery(id+"F1.wireOp",EDGE,"E51.19.0");Q19=makeQuery(id+"F1.imprint","IMPRINT",FACE,{"disambiguationData":[TD([[makeQuery(id+"F1.imprint","IMPRINT",EDGE,{"derivedFrom":subQ8}),-1.0]])]});}
            var Q20;
            {var subQ8=sQuery(id+"F1.wireOp",EDGE,"E21");Q20=makeQuery(id+"F1.imprint","IMPRINT",FACE,{"disambiguationData":[TD([[makeQuery(id+"F1.imprint","IMPRINT",EDGE,{"derivedFrom":subQ8}),-1.0]])]});}
            extrude(context, id + "F2", {"entities" : qUnion([Q0, Q1, Q2, Q3, Q4, Q5, Q6, Q7, Q8, Q9, Q10, Q11, Q12, Q13, Q14, Q15, Q16, Q17, Q18, Q19, Q20]), "depth" : (getVariable(context, 'GearThickness')) * mm});
        }
    });
